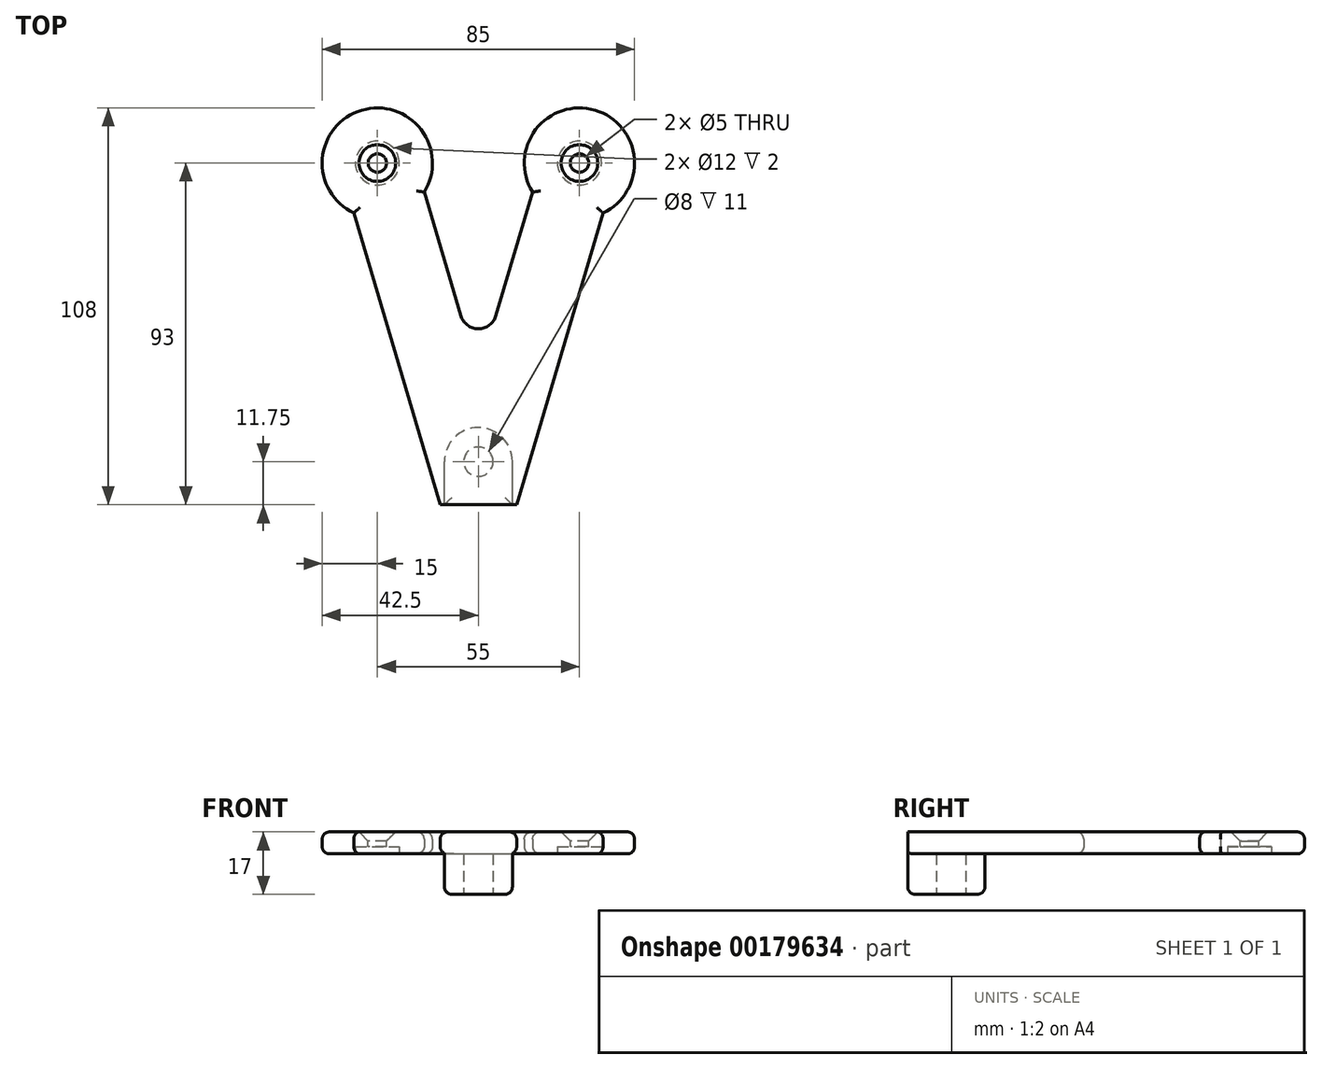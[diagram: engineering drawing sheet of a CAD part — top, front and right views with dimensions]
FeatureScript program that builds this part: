
annotation { "Feature Type Name" : "Feature", "Feature Type Description" : "" }
export const myFeature = defineFeature(function(context is Context, id is Id, definition is map)
    precondition{}
    {
        {
            var Q0;
            Q0=qCreatedBy(makeId("Top.planeOp"),FACE);
            var sketch = newSketch(context, id + "F0", { "sketchPlane" : qUnion([Q0])});
            skLineSegment(sketch, "E0", {"start": v(0, 0) * mm, "end": v(10.43, 0) * mm});
            skLineSegment(sketch, "E1", {"start": v(0, 0) * mm, "end": v(-10.43, 0) * mm});
            skArc(sketch, "E2", {"start": v(33.92, 79.44) * mm, "mid": v(31.75, 107.38) * mm, "end": v(14.74, 85.11) * mm});
            skArc(sketch, "E3", {"start": v(-14.74, 85.11) * mm, "mid": v(-31.75, 107.38) * mm, "end": v(-33.92, 79.44) * mm});
            skLineSegment(sketch, "E4.0", {"start": v(10.43, 0) * mm, "end": v(33.92, 79.44) * mm});
            skLineSegment(sketch, "E5.0", {"start": v(4.8, 51.48) * mm, "end": v(14.74, 85.11) * mm});
            skLineSegment(sketch, "E6.0", {"start": v(-10.43, 0) * mm, "end": v(-33.92, 79.44) * mm});
            skLineSegment(sketch, "E7.0", {"start": v(-4.8, 51.48) * mm, "end": v(-14.74, 85.11) * mm});
            skArc(sketch, "E8.filletArc", {"start": v(-4.8, 51.48) * mm, "mid": v(0, 47.9) * mm, "end": v(4.8, 51.48) * mm});
            skPoint(sketch, "E9.orphan", {"position": v(-10, 0) * mm});
            skSolve(sketch);
        }
        {
            var Q0;
            Q0=makeQuery(id+"F0.imprint","IMPRINT",FACE,{"disambiguationData":[TD([[makeQuery(id+"F0.imprint","IMPRINT",EDGE,{"derivedFrom":sQuery(id+"F0.wireOp",EDGE,"E0")}),1.0]])]});
            extrude(context, id + "F1", {"entities" : qUnion([Q0]), "depth" : 6 * mm});
        }
        {
            var Q0;
            Q0=makeQuery(id+"F1.opExtrude","CAP_FACE",FACE,{"disambiguationData":[OSD([sQuery(id+"F0.wireOp",EDGE,"E0"),sQuery(id+"F0.wireOp",EDGE,"E1"),sQuery(id+"F0.wireOp",EDGE,"E2"),sQuery(id+"F0.wireOp",EDGE,"E3"),sQuery(id+"F0.wireOp",EDGE,"E4.0"),sQuery(id+"F0.wireOp",EDGE,"E5.0"),sQuery(id+"F0.wireOp",EDGE,"E6.0"),sQuery(id+"F0.wireOp",EDGE,"E7.0"),sQuery(id+"F0.wireOp",EDGE,"E8.filletArc")])],"isStart":true});
            var sketch = newSketch(context, id + "F2", { "sketchPlane" : qUnion([Q0])});
            skLineSegment(sketch, "E10.bottom", {"start": v(0, 0) * mm, "end": v(9.25, 0) * mm});
            skLineSegment(sketch, "E10.top", {"start": v(0, -21) * mm, "end": v(0, -21) * mm});
            skLineSegment(sketch, "E10.right", {"start": v(9.25, 0) * mm, "end": v(9.25, -11.75) * mm});
            skLineSegment(sketch, "E11.bottom", {"start": v(0, 0) * mm, "end": v(-9.25, 0) * mm});
            skLineSegment(sketch, "E11.right", {"start": v(-9.25, 0) * mm, "end": v(-9.25, -11.75) * mm});
            skPoint(sketch, "E12.visualSharp", {"position": v(9.25, -21) * mm});
            skArc(sketch, "E12.filletArc", {"start": v(0, -21) * mm, "mid": v(6.54, -18.3) * mm, "end": v(9.25, -11.75) * mm});
            skPoint(sketch, "E13.visualSharp", {"position": v(-9.25, -21) * mm});
            skArc(sketch, "E13.filletArc", {"start": v(-9.25, -11.75) * mm, "mid": v(-6.54, -18.3) * mm, "end": v(0, -21) * mm});
            skSolve(sketch);
        }
        {
            var Q0;
            Q0=makeQuery(id+"F2.imprint","IMPRINT",FACE,{"disambiguationData":[TD([[makeQuery(id+"F2.imprint","IMPRINT",EDGE,{"derivedFrom":sQuery(id+"F2.wireOp",EDGE,"E10.bottom")}),1.0]])]});
            extrude(context, id + "F3", {"entities" : qUnion([Q0]), "operationType" : NewBodyOperationType.ADD, "depth" : 11 * mm});
        }
        {
            var Q0;
            Q0=makeQuery(id+"F1.opExtrude","CAP_FACE",FACE,{"disambiguationData":[OSD([sQuery(id+"F0.wireOp",EDGE,"E0"),sQuery(id+"F0.wireOp",EDGE,"E1"),sQuery(id+"F0.wireOp",EDGE,"E2"),sQuery(id+"F0.wireOp",EDGE,"E3"),sQuery(id+"F0.wireOp",EDGE,"E4.0"),sQuery(id+"F0.wireOp",EDGE,"E5.0"),sQuery(id+"F0.wireOp",EDGE,"E6.0"),sQuery(id+"F0.wireOp",EDGE,"E7.0"),sQuery(id+"F0.wireOp",EDGE,"E8.filletArc")])],"isStart":false});
            var sketch = newSketch(context, id + "F4", { "sketchPlane" : qUnion([Q0])});
            skCircle(sketch, "E14", {"center": v(27.5, 93) * mm, "radius": 2.5 * mm});
            skCircle(sketch, "E15", {"center": v(-27.5, 93) * mm, "radius": 2.5 * mm});
            skSolve(sketch);
        }
        {
            var Q0;
            Q0=sQuery(id+"F4.wireOp",VERTEX,"E14.center");
            var Q1;
            Q1=sQuery(id+"F4.wireOp",VERTEX,"E15.center");
            var Q2;
            Q2=makeQuery(id+"F1.opExtrude","SWEPT_BODY",BODY,{"disambiguationData":[OSD([sQuery(id+"F0.wireOp",EDGE,"E0"),sQuery(id+"F0.wireOp",EDGE,"E1"),sQuery(id+"F0.wireOp",EDGE,"E2"),sQuery(id+"F0.wireOp",EDGE,"E3"),sQuery(id+"F0.wireOp",EDGE,"E4.0"),sQuery(id+"F0.wireOp",EDGE,"E5.0"),sQuery(id+"F0.wireOp",EDGE,"E6.0"),sQuery(id+"F0.wireOp",EDGE,"E7.0"),sQuery(id+"F0.wireOp",EDGE,"E8.filletArc")])]});
            hole(context, id + "F5", {"style" : HoleStyle.C_SINK, "endStyle" : HoleEndStyle.THROUGH, "holeDiameter" : 5 * mm, "cSinkDiameter" : 10 * mm, "cSinkAngle" : 90 * degree, "locations" : qUnion([Q0, Q1]), "scope" : qUnion([Q2]), "isTappedThrough" : true});
        }
        {
            var Q0;
            Q0=makeQuery(id+"F1.opExtrude","CAP_FACE",FACE,{"disambiguationData":[OSD([sQuery(id+"F0.wireOp",EDGE,"E0"),sQuery(id+"F0.wireOp",EDGE,"E1"),sQuery(id+"F0.wireOp",EDGE,"E2"),sQuery(id+"F0.wireOp",EDGE,"E3"),sQuery(id+"F0.wireOp",EDGE,"E4.0"),sQuery(id+"F0.wireOp",EDGE,"E5.0"),sQuery(id+"F0.wireOp",EDGE,"E6.0"),sQuery(id+"F0.wireOp",EDGE,"E7.0"),sQuery(id+"F0.wireOp",EDGE,"E8.filletArc")])],"isStart":true});
            var sketch = newSketch(context, id + "F6", { "sketchPlane" : qUnion([Q0])});
            skCircle(sketch, "E16", {"center": v(27.5, -93) * mm, "radius": 6 * mm});
            skCircle(sketch, "E17", {"center": v(-27.5, -93) * mm, "radius": 6 * mm});
            skSolve(sketch);
        }
        {
            var Q0;
            Q0=makeQuery(id+"F6.imprint","IMPRINT",FACE,{"disambiguationData":[TD([[makeQuery(id+"F6.imprint","IMPRINT",EDGE,{"derivedFrom":sQuery(id+"F6.wireOp",EDGE,"E16")}),1.0]])]});
            var Q1;
            Q1=makeQuery(id+"F6.imprint","IMPRINT",FACE,{"disambiguationData":[TD([[makeQuery(id+"F6.imprint","IMPRINT",EDGE,{"derivedFrom":sQuery(id+"F6.wireOp",EDGE,"E17")}),1.0]])]});
            extrude(context, id + "F7", {"entities" : qUnion([Q0, Q1]), "operationType" : NewBodyOperationType.REMOVE, "oppositeDirection" : true, "depth" : 2 * mm});
        }
        {
            var Q0;
            Q0=makeQuery(id+"F1.opExtrude","CAP_EDGE",EDGE,{"disambiguationData":[OSD([sQuery(id+"F0.wireOp",EDGE,"E4.0")])],"isStart":true});
            var Q1;
            Q1=makeQuery(id+"F1.opExtrude","CAP_EDGE",EDGE,{"disambiguationData":[OSD([sQuery(id+"F0.wireOp",EDGE,"E2")])],"isStart":true});
            var Q2;
            Q2=makeQuery(id+"F1.opExtrude","CAP_EDGE",EDGE,{"disambiguationData":[OSD([sQuery(id+"F0.wireOp",EDGE,"E5.0")])],"isStart":false});
            var Q3;
            Q3=makeQuery(id+"F1.opExtrude","CAP_EDGE",EDGE,{"disambiguationData":[OSD([sQuery(id+"F0.wireOp",EDGE,"E8.filletArc")])],"isStart":true});
            var Q4;
            Q4=makeQuery(id+"F1.opExtrude","CAP_EDGE",EDGE,{"disambiguationData":[OSD([sQuery(id+"F0.wireOp",EDGE,"E7.0")])],"isStart":true});
            var Q5;
            Q5=makeQuery(id+"F1.opExtrude","CAP_EDGE",EDGE,{"disambiguationData":[OSD([sQuery(id+"F0.wireOp",EDGE,"E3")])],"isStart":true});
            var Q6;
            Q6=makeQuery(id+"F1.opExtrude","CAP_EDGE",EDGE,{"disambiguationData":[OSD([sQuery(id+"F0.wireOp",EDGE,"E6.0")])],"isStart":true});
            var Q7;
            Q7=makeQuery(id+"F3.opExtrude","CAP_EDGE",EDGE,{"disambiguationData":[OSD([sQuery(id+"F2.wireOp",EDGE,"E11.right")])],"isStart":false});
            var Q8;
            Q8=makeQuery(id+"F3.opExtrude","CAP_EDGE",EDGE,{"disambiguationData":[OSD([sQuery(id+"F2.wireOp",EDGE,"E10.bottom"),sQuery(id+"F2.wireOp",EDGE,"E11.bottom")])],"isStart":false});
            var Q9;
            Q9=makeQuery(id+"F1.opExtrude","CAP_EDGE",EDGE,{"disambiguationData":[OSD([sQuery(id+"F0.wireOp",EDGE,"E3")])],"isStart":false});
            var Q10;
            Q10=makeQuery(id+"F1.opExtrude","CAP_EDGE",EDGE,{"disambiguationData":[OSD([sQuery(id+"F0.wireOp",EDGE,"E6.0")])],"isStart":false});
            var Q11;
            Q11=makeQuery(id+"F1.opExtrude","CAP_EDGE",EDGE,{"disambiguationData":[OSD([sQuery(id+"F0.wireOp",EDGE,"E4.0")])],"isStart":false});
            var Q12;
            Q12=makeQuery(id+"F1.opExtrude","CAP_EDGE",EDGE,{"disambiguationData":[OSD([sQuery(id+"F0.wireOp",EDGE,"E2")])],"isStart":false});
            fillet(context, id + "F8", {"entities" : qUnion([Q0, Q1, Q2, Q3, Q4, Q5, Q6, Q7, Q8, Q9, Q10, Q11, Q12]), "radius" : 2 * mm, "tangentPropagation" : true, "allowEdgeOverflow" : false});
        }
        {
            var Q0;
            Q0=makeQuery(id+"F3.opExtrude","CAP_FACE",FACE,{"disambiguationData":[OSD([sQuery(id+"F2.wireOp",EDGE,"E10.bottom"),sQuery(id+"F2.wireOp",EDGE,"E10.right"),sQuery(id+"F2.wireOp",EDGE,"E11.bottom"),sQuery(id+"F2.wireOp",EDGE,"E11.right"),sQuery(id+"F2.wireOp",EDGE,"E12.filletArc"),sQuery(id+"F2.wireOp",EDGE,"E13.filletArc")])],"isStart":false});
            var sketch = newSketch(context, id + "F9", { "sketchPlane" : qUnion([Q0])});
            skCircle(sketch, "E18", {"center": v(0, -11.75) * mm, "radius": 4 * mm});
            skSolve(sketch);
        }
        {
            var Q0;
            Q0=makeQuery(id+"F9.imprint","IMPRINT",FACE,{"disambiguationData":[TD([[makeQuery(id+"F9.imprint","IMPRINT",EDGE,{"derivedFrom":sQuery(id+"F9.wireOp",EDGE,"E18")}),1.0]])]});
            extrude(context, id + "F10", {"entities" : qUnion([Q0]), "operationType" : NewBodyOperationType.REMOVE, "oppositeDirection" : true, "depth" : 11 * mm});
        }
    });
